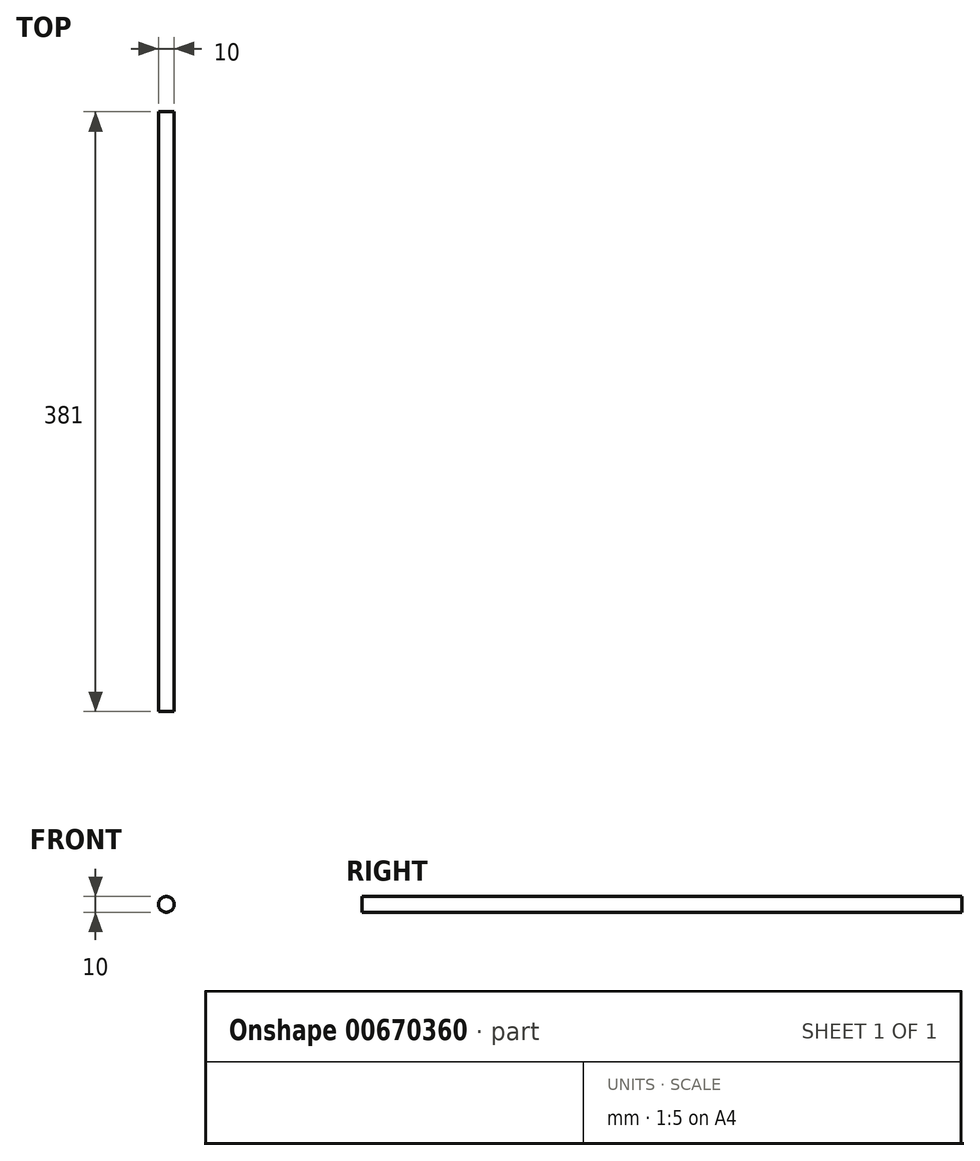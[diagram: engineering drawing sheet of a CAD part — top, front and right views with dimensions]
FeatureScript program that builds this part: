
annotation { "Feature Type Name" : "Feature", "Feature Type Description" : "" }
export const myFeature = defineFeature(function(context is Context, id is Id, definition is map)
    precondition{}
    {
        {
            var Q0;
            Q0=qCreatedBy(makeId("Front.planeOp"),FACE);
            var sketch = newSketch(context, id + "F0", { "sketchPlane" : qUnion([Q0])});
            skCircle(sketch, "E0", {"center": v(0, 0) * mm, "radius": 5 * mm});
            skSolve(sketch);
        }
        {
            var Q0;
            Q0=makeQuery(id+"F0.imprint","IMPRINT",FACE,{"disambiguationData":[TD([[makeQuery(id+"F0.imprint","IMPRINT",EDGE,{"derivedFrom":sQuery(id+"F0.wireOp",EDGE,"E0")}),1.0]])]});
            extrude(context, id + "F1", {"entities" : qUnion([Q0]), "depth" : 381 * mm, "offsetDistance" : 25.4 * mm});
        }
    });
